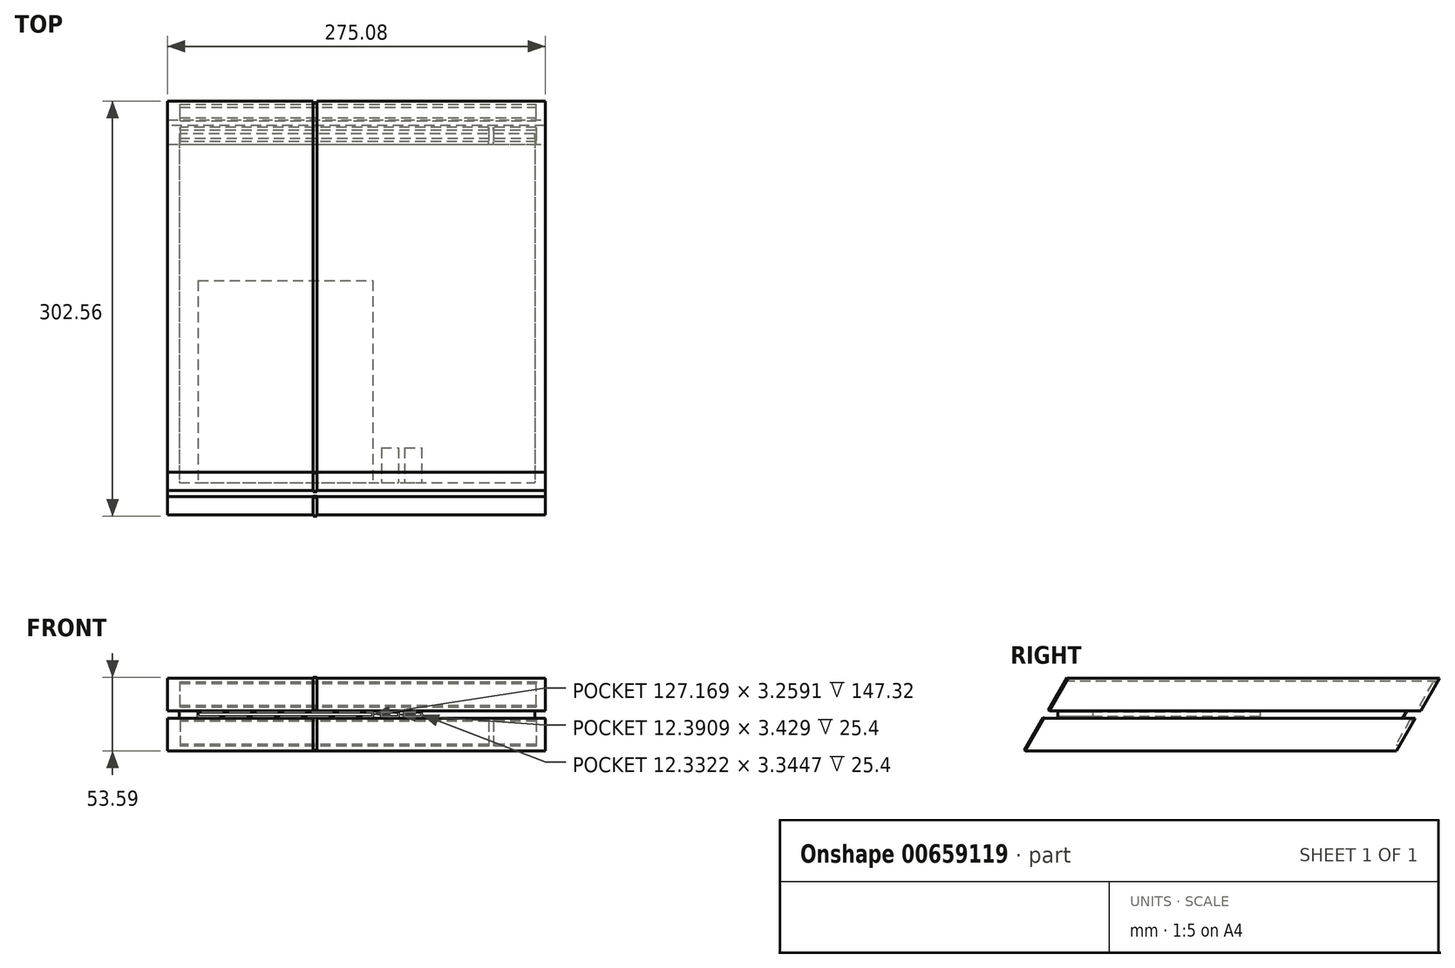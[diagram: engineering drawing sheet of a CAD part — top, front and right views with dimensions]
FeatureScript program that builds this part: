
annotation { "Feature Type Name" : "Feature", "Feature Type Description" : "" }
export const myFeature = defineFeature(function(context is Context, id is Id, definition is map)
    precondition{}
    {
        {
            var Q0;
            Q0=qCreatedBy(makeId("Top.planeOp"),FACE);
            var sketch = newSketch(context, id + "F0", { "sketchPlane" : qUnion([Q0])});
            skLineSegment(sketch, "E0.bottom", {"start": v(-137.54, 152.53) * mm, "end": v(137.54, 152.53) * mm});
            skLineSegment(sketch, "E0.top", {"start": v(-137.54, -152.53) * mm, "end": v(137.54, -152.53) * mm});
            skLineSegment(sketch, "E0.left", {"start": v(-137.54, 152.53) * mm, "end": v(-137.54, -152.53) * mm});
            skLineSegment(sketch, "E0.right", {"start": v(137.54, 152.53) * mm, "end": v(137.54, -152.53) * mm});
            skPoint(sketch, "E0.middle", {"position": v(0, 0) * mm});
            skSolve(sketch);
        }
        {
            var Q0;
            Q0=qSketchRegion(id+"F0",true);
            extrude(context, id + "F1", {"entities" : qUnion([Q0]), "depth" : 23.88 * mm, "offsetDistance" : 25.4 * mm});
        }
        {
            var Q0;
            Q0=makeQuery(id+"F1.opExtrude","CAP_EDGE",EDGE,{"disambiguationData":[OSD([sQuery(id+"F0.wireOp",EDGE,"E0.top")])],"isStart":false});
            chamfer(context, id + "F2", {"entities" : qUnion([Q0]), "chamferType" : ChamferType.OFFSET_ANGLE, "width" : 24.13 * mm, "oppositeDirection" : false, "angle" : 60.33 * degree, "tangentPropagation" : true});
        }
        {
            var Q0;
            Q0=makeQuery(id+"F1.opExtrude","CAP_EDGE",EDGE,{"disambiguationData":[OSD([sQuery(id+"F0.wireOp",EDGE,"E0.bottom")])],"isStart":true});
            chamfer(context, id + "F3", {"entities" : qUnion([Q0]), "chamferType" : ChamferType.OFFSET_ANGLE, "width" : 24.13 * mm, "oppositeDirection" : false, "angle" : 60.33 * degree, "tangentPropagation" : true});
        }
        {
            var Q0;
            Q0=makeQuery(id+"F1.opExtrude","CAP_FACE",FACE,{"disambiguationData":[OSD([sQuery(id+"F0.wireOp",EDGE,"E0.bottom"),sQuery(id+"F0.wireOp",EDGE,"E0.top"),sQuery(id+"F0.wireOp",EDGE,"E0.left"),sQuery(id+"F0.wireOp",EDGE,"E0.right")])],"isStart":false});
            var sketch = newSketch(context, id + "F4", { "sketchPlane" : qUnion([Q0])});
            skLineSegment(sketch, "E1.bottom", {"start": v(-129.05, 135.9) * mm, "end": v(130.03, 135.9) * mm});
            skLineSegment(sketch, "E1.top", {"start": v(-129.05, -118.35) * mm, "end": v(130.03, -118.35) * mm});
            skLineSegment(sketch, "E1.left", {"start": v(-129.05, 135.9) * mm, "end": v(-129.05, -118.35) * mm});
            skLineSegment(sketch, "E1.right", {"start": v(130.03, 135.9) * mm, "end": v(130.03, -118.35) * mm});
            skSolve(sketch);
        }
        {
            var Q0;
            Q0=qSketchRegion(id+"F4",true);
            extrude(context, id + "F5", {"entities" : qUnion([Q0]), "depth" : 5.33 * mm, "offsetDistance" : 25.4 * mm});
        }
        {
            var Q0;
            Q0=makeQuery(id+"F1.opExtrude","SWEPT_BODY",BODY,{"disambiguationData":[OSD([sQuery(id+"F0.wireOp",EDGE,"E0.bottom"),sQuery(id+"F0.wireOp",EDGE,"E0.top"),sQuery(id+"F0.wireOp",EDGE,"E0.left"),sQuery(id+"F0.wireOp",EDGE,"E0.right")])]});
            transform(context, id + "F6", {"entities" : qUnion([Q0]), "transformType" : TransformType.TRANSLATION_3D, "dx" : 0 * mm, "dy" : 17.78 * mm, "dz" : 29.2 * mm, "makeCopy" : true});
        }
        {
            var Q0;
            Q0=makeQuery(id+"F6.opPattern","COPY",FACE,{"derivedFrom":makeQuery(id+"F3.opChamfer","BLEND_FACE",FACE,{"disambiguationData":[OSD([sQuery(id+"F0.wireOp",EDGE,"E0.bottom")])]}),"instanceName":"1"});
            var sketch = newSketch(context, id + "F7", { "sketchPlane" : qUnion([Q0])});
            skLineSegment(sketch, "E2.bottom", {"start": v(128.5, 101.05) * mm, "end": v(-131.1, 101.05) * mm});
            skLineSegment(sketch, "E2.top", {"start": v(128.5, 120.6) * mm, "end": v(-131.1, 120.6) * mm});
            skLineSegment(sketch, "E2.left", {"start": v(128.5, 101.05) * mm, "end": v(128.5, 120.6) * mm});
            skLineSegment(sketch, "E2.right", {"start": v(-131.1, 101.05) * mm, "end": v(-131.1, 120.6) * mm});
            skSolve(sketch);
        }
        {
            var Q0;
            Q0=qSketchRegion(id+"F7",true);
            extrude(context, id + "F8", {"entities" : qUnion([Q0]), "operationType" : NewBodyOperationType.REMOVE, "oppositeDirection" : true, "depth" : 2.54 * mm, "offsetDistance" : 25.4 * mm});
        }
        {
            var Q0;
            Q0=makeQuery(id+"F3.opChamfer","BLEND_FACE",FACE,{"disambiguationData":[OSD([sQuery(id+"F0.wireOp",EDGE,"E0.bottom")])]});
            var sketch = newSketch(context, id + "F9", { "sketchPlane" : qUnion([Q0])});
            skLineSegment(sketch, "E3.bottom", {"start": v(-131.1, 88.23) * mm, "end": v(-100.01, 88.23) * mm});
            skLineSegment(sketch, "E3.top", {"start": v(-131.1, 67.37) * mm, "end": v(-100.01, 67.37) * mm});
            skLineSegment(sketch, "E3.left", {"start": v(-131.1, 88.23) * mm, "end": v(-131.1, 67.37) * mm});
            skLineSegment(sketch, "E3.right", {"start": v(-100.01, 88.23) * mm, "end": v(-100.01, 67.37) * mm});
            skPoint(sketch, "E4.oppositeSnap0", {"position": v(-115.55, 67.37) * mm});
            skLineSegment(sketch, "E4.bottom", {"start": v(-96.27, 88.23) * mm, "end": v(128.5, 88.23) * mm});
            skLineSegment(sketch, "E4.top", {"start": v(-96.27, 67.37) * mm, "end": v(128.5, 67.37) * mm});
            skLineSegment(sketch, "E4.left", {"start": v(-96.27, 88.23) * mm, "end": v(-96.27, 67.37) * mm});
            skLineSegment(sketch, "E4.right", {"start": v(128.5, 88.23) * mm, "end": v(128.5, 67.37) * mm});
            skSolve(sketch);
        }
        {
            var Q0;
            Q0=qSketchRegion(id+"F9",true);
            extrude(context, id + "F10", {"entities" : qUnion([Q0]), "operationType" : NewBodyOperationType.REMOVE, "oppositeDirection" : true, "depth" : 2.54 * mm, "offsetDistance" : 25.4 * mm});
        }
        {
            var Q0;
            Q0=makeQuery(id+"F6.opPattern","COPY",FACE,{"derivedFrom":makeQuery(id+"F1.opExtrude","CAP_FACE",FACE,{"disambiguationData":[OSD([sQuery(id+"F0.wireOp",EDGE,"E0.bottom"),sQuery(id+"F0.wireOp",EDGE,"E0.top"),sQuery(id+"F0.wireOp",EDGE,"E0.left"),sQuery(id+"F0.wireOp",EDGE,"E0.right")])],"isStart":false}),"instanceName":"1"});
            var sketch = newSketch(context, id + "F11", { "sketchPlane" : qUnion([Q0])});
            skLineSegment(sketch, "E5.bottom", {"start": v(-137.54, 159.78) * mm, "end": v(-31.7, 159.78) * mm});
            skLineSegment(sketch, "E5.top", {"start": v(-137.54, -110.62) * mm, "end": v(-31.7, -110.62) * mm});
            skLineSegment(sketch, "E5.left", {"start": v(-137.54, 159.78) * mm, "end": v(-137.54, -110.62) * mm});
            skLineSegment(sketch, "E5.right", {"start": v(-31.7, 159.78) * mm, "end": v(-31.7, -110.62) * mm});
            skSolve(sketch);
        }
        {
            var Q0;
            {var subQ0=sQuery(id+"F11.wireOp",EDGE,"E5.right");Q0=makeQuery(id+"F11.imprint","IMPRINT",FACE,{"disambiguationData":[TD([[makeQuery(id+"F11.imprint","IMPRINT",EDGE,{"derivedFrom":subQ0}),1.0]])]});}
            var sketch = newSketch(context, id + "F12", { "sketchPlane" : qUnion([Q0])});
            skLineSegment(sketch, "E6.bottom", {"start": v(-28.64, 161.76) * mm, "end": v(-31.64, 161.76) * mm});
            skLineSegment(sketch, "E6.top", {"start": v(-28.64, -112.56) * mm, "end": v(-31.64, -112.56) * mm});
            skLineSegment(sketch, "E6.left", {"start": v(-28.64, 161.76) * mm, "end": v(-28.64, -112.56) * mm});
            skLineSegment(sketch, "E6.right", {"start": v(-31.64, 161.76) * mm, "end": v(-31.64, -112.56) * mm});
            skSolve(sketch);
        }
        {
            var Q0;
            Q0=qSketchRegion(id+"F12",true);
            extrude(context, id + "F13", {"entities" : qUnion([Q0]), "operationType" : NewBodyOperationType.REMOVE, "oppositeDirection" : true, "depth" : 2.3 * mm, "offsetDistance" : 25.4 * mm});
        }
        {
            var Q0;
            Q0=makeQuery(id+"F6.opPattern","COPY",FACE,{"derivedFrom":makeQuery(id+"F2.opChamfer","BLEND_FACE",FACE,{"disambiguationData":[OSD([sQuery(id+"F0.wireOp",EDGE,"E0.top")])]}),"instanceName":"1"});
            var sketch = newSketch(context, id + "F14", { "sketchPlane" : qUnion([Q0])});
            skLineSegment(sketch, "E7.bottom", {"start": v(-31.64, -8.63) * mm, "end": v(-28.64, -8.63) * mm});
            skLineSegment(sketch, "E7.top", {"start": v(-31.64, -36.1) * mm, "end": v(-28.64, -36.1) * mm});
            skLineSegment(sketch, "E7.left", {"start": v(-31.64, -8.63) * mm, "end": v(-31.64, -36.1) * mm});
            skLineSegment(sketch, "E7.right", {"start": v(-28.64, -8.63) * mm, "end": v(-28.64, -36.1) * mm});
            skSolve(sketch);
        }
        {
            var Q0;
            Q0=qSketchRegion(id+"F14",true);
            extrude(context, id + "F15", {"entities" : qUnion([Q0]), "depth" : 1.02 * mm, "offsetDistance" : 25.4 * mm});
        }
        {
            var Q0;
            Q0=makeQuery(id+"F15.opExtrude","SWEPT_BODY",BODY,{"disambiguationData":[OSD([sQuery(id+"F14.wireOp",EDGE,"E7.bottom"),sQuery(id+"F14.wireOp",EDGE,"E7.top"),sQuery(id+"F14.wireOp",EDGE,"E7.left"),sQuery(id+"F14.wireOp",EDGE,"E7.right")])]});
            transform(context, id + "F16", {"entities" : qUnion([Q0]), "transformType" : TransformType.TRANSLATION_3D, "dx" : 0 * mm, "dy" : -17.68 * mm, "dz" : -29.08 * mm, "makeCopy" : true});
        }
        {
            var Q0;
            Q0=makeQuery(id+"F5.opExtrude","SWEPT_FACE",FACE,{"disambiguationData":[OSD([sQuery(id+"F4.wireOp",EDGE,"E1.top")])]});
            var sketch = newSketch(context, id + "F17", { "sketchPlane" : qUnion([Q0])});
            skLineSegment(sketch, "E8.bottom", {"start": v(-115.25, 28.17) * mm, "end": v(11.92, 28.17) * mm});
            skLineSegment(sketch, "E8.top", {"start": v(-115.25, 24.91) * mm, "end": v(11.92, 24.91) * mm});
            skLineSegment(sketch, "E8.left", {"start": v(-115.25, 28.17) * mm, "end": v(-115.25, 24.91) * mm});
            skLineSegment(sketch, "E8.right", {"start": v(11.92, 28.17) * mm, "end": v(11.92, 24.91) * mm});
            skSolve(sketch);
        }
        {
            var Q0;
            Q0=qSketchRegion(id+"F17",true);
            extrude(context, id + "F18", {"entities" : qUnion([Q0]), "operationType" : NewBodyOperationType.REMOVE, "oppositeDirection" : true, "depth" : 147.32 * mm, "offsetDistance" : 25.4 * mm});
        }
        {
            var Q0;
            Q0=makeQuery(id+"F5.opExtrude","SWEPT_FACE",FACE,{"disambiguationData":[OSD([sQuery(id+"F4.wireOp",EDGE,"E1.top")])]});
            var sketch = newSketch(context, id + "F19", { "sketchPlane" : qUnion([Q0])});
            skLineSegment(sketch, "E9.bottom", {"start": v(18.18, 28.3) * mm, "end": v(30.57, 28.3) * mm});
            skLineSegment(sketch, "E9.top", {"start": v(18.18, 24.87) * mm, "end": v(30.57, 24.87) * mm});
            skLineSegment(sketch, "E9.left", {"start": v(18.18, 28.3) * mm, "end": v(18.18, 24.87) * mm});
            skLineSegment(sketch, "E9.right", {"start": v(30.57, 28.3) * mm, "end": v(30.57, 24.87) * mm});
            skSolve(sketch);
        }
        {
            var Q0;
            Q0=makeQuery(id+"F19.imprint","IMPRINT",FACE,{"disambiguationData":[TD([[makeQuery(id+"F19.imprint","IMPRINT",EDGE,{"derivedFrom":sQuery(id+"F19.wireOp",EDGE,"E9.bottom")}),-1.0]])]});
            extrude(context, id + "F20", {"entities" : qUnion([Q0]), "operationType" : NewBodyOperationType.REMOVE, "oppositeDirection" : true, "depth" : 25.4 * mm, "offsetDistance" : 25.4 * mm});
        }
        {
            var Q0;
            Q0=makeQuery(id+"F5.opExtrude","SWEPT_FACE",FACE,{"disambiguationData":[OSD([sQuery(id+"F4.wireOp",EDGE,"E1.top")])]});
            var sketch = newSketch(context, id + "F21", { "sketchPlane" : qUnion([Q0])});
            skLineSegment(sketch, "E10.bottom", {"start": v(35.26, 28.26) * mm, "end": v(47.6, 28.26) * mm});
            skLineSegment(sketch, "E10.top", {"start": v(35.26, 24.91) * mm, "end": v(47.6, 24.91) * mm});
            skLineSegment(sketch, "E10.left", {"start": v(35.26, 28.26) * mm, "end": v(35.26, 24.91) * mm});
            skLineSegment(sketch, "E10.right", {"start": v(47.6, 28.26) * mm, "end": v(47.6, 24.91) * mm});
            skSolve(sketch);
        }
        {
            var Q0;
            Q0=qSketchRegion(id+"F21",true);
            extrude(context, id + "F22", {"entities" : qUnion([Q0]), "operationType" : NewBodyOperationType.REMOVE, "oppositeDirection" : true, "depth" : 25.4 * mm, "offsetDistance" : 25.4 * mm});
        }
        {
            var Q0;
            Q0=makeQuery(id+"F5.opExtrude","CAP_EDGE",EDGE,{"disambiguationData":[OSD([sQuery(id+"F4.wireOp",EDGE,"E1.bottom")])],"isStart":true});
            chamfer(context, id + "F23", {"entities" : qUnion([Q0]), "chamferType" : ChamferType.OFFSET_ANGLE, "width" : 3.05 * mm, "oppositeDirection" : false, "angle" : 60.33 * degree, "tangentPropagation" : true});
        }
    });
